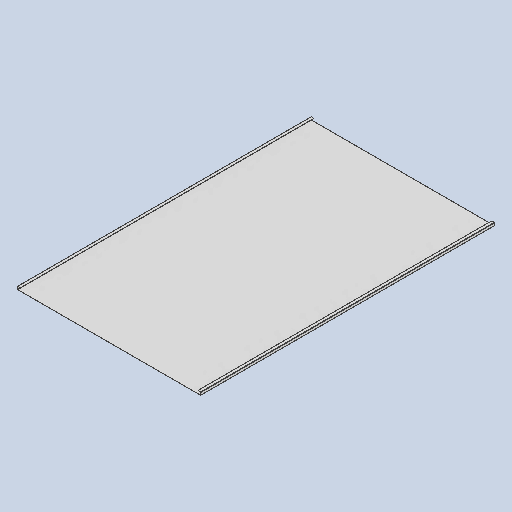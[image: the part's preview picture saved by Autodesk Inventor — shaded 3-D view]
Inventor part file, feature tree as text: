
AUTODESK INVENTOR PART (.ipt)
format: ipt  version: 2025 (Build 290162010, 162A)  size: 334,848 bytes
history: native  units: mm
features: sheet_metal_op x13, other x6, sketch x5, chamfer x1
ambient origin geometry x8: Origin, YZ Plane, XZ Plane, XY Plane, X Axis, Y Axis, Z Axis, Center Point
bodies: Body1 (feature_tree)
feature tree (25):
  sheet_metal_op  "Face1"
  sheet_metal_op  "Flange2"
  sheet_metal_op  "Flange3"
  sheet_metal_op  "Flange4"
  sheet_metal_op  "Flange5"
  chamfer  "Corner Round1"
  sketch  "Sketch6"  dims[d12=23.212879mm]
  other  "Plate2"
  sketch  "Sketch11"  dims[d52=612.6mm]
  other  "Plate4"
  sheet_metal_op  "Bend3"
  sheet_metal_op  "Corner3"
  sketch  "Sketch12"  dims[d53=980.0mm]
  other  "Plate5"
  sheet_metal_op  "Bend4"
  sheet_metal_op  "Corner4"
  sketch  "Sketch13"  dims[d54=0.5mm]
  other  "Plate6"
  sheet_metal_op  "Bend5"
  sheet_metal_op  "Corner5"
  sketch  "Sketch14"  dims[d84=0.5mm d85=0.25mm d86=1.0mm d87=0.5mm d88=10.0mm d89=90.0deg d90=0.5mm d91=2.0mm d92=0.5mm d93=0.5mm d94=0.5mm d95=0.25mm d96=1.0mm d97=0.5mm d98=10.0mm d99=90.0deg d100=0.5mm d101=2.0mm d102=0.5mm d103=0.5mm d104=0.5mm d105=0.25mm d106=1.0mm d107=0.5mm d108=10.0mm d109=90.0deg d110=0.5mm d111=2.0mm d112=0.5mm d113=0.5mm d114=0.5mm d115=0.25mm d116=1.0mm d117=0.5mm d118=10.0mm d119=90.0deg d120=0.5mm d121=2.0mm d122=0.5mm d123=0.5mm d124=4.0mm]
  other  "Plate7"
  sheet_metal_op  "Bend6"
  sheet_metal_op  "Corner6"
  other  "Definition1"
